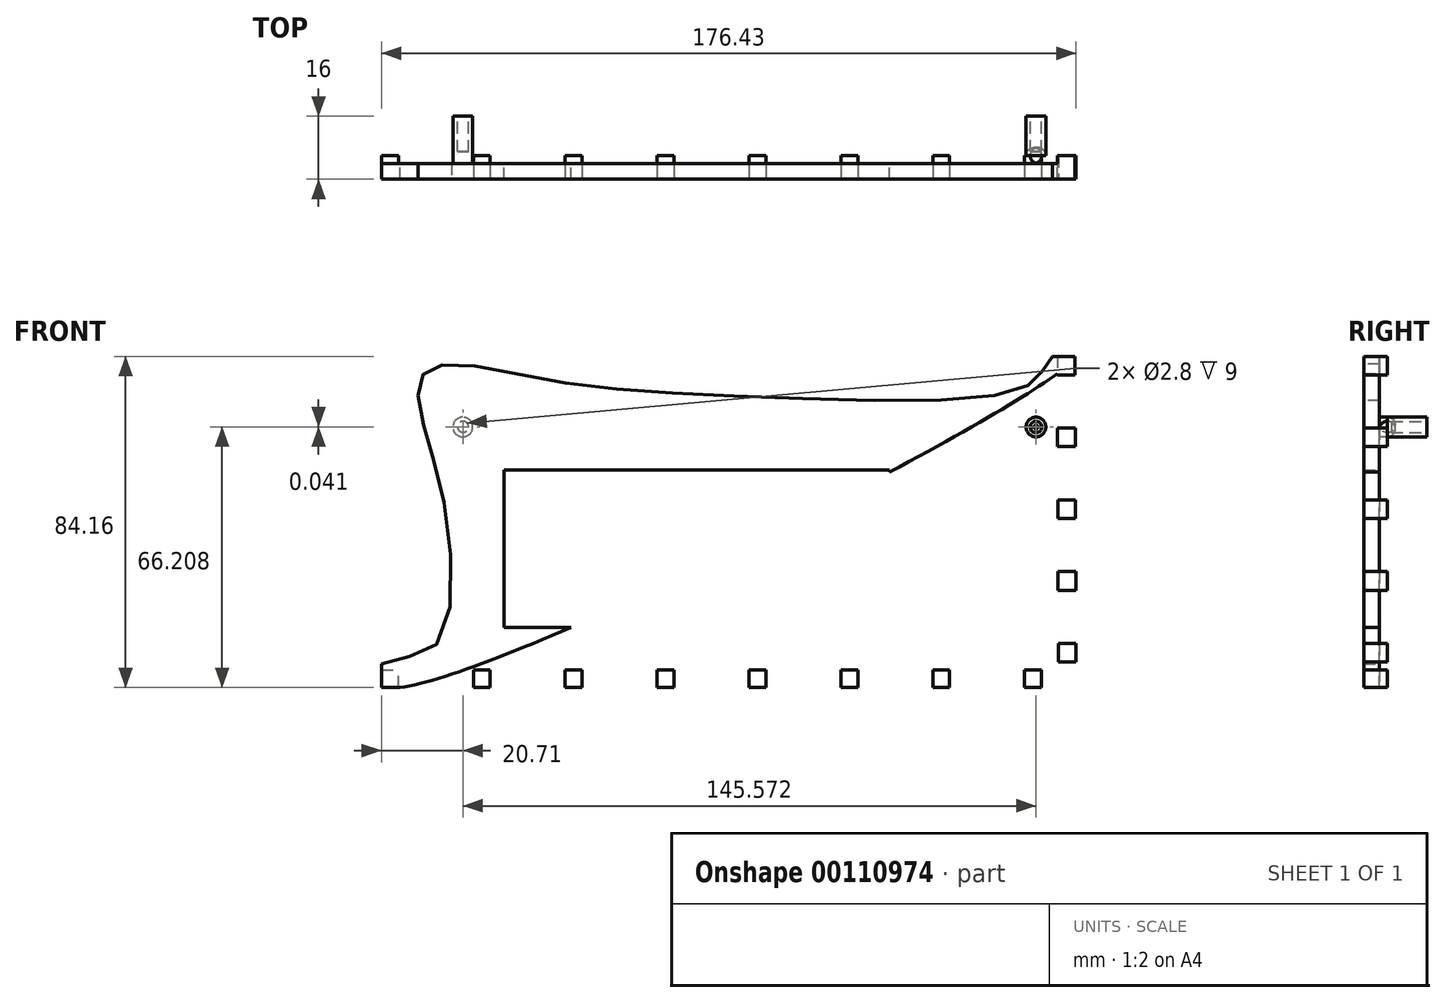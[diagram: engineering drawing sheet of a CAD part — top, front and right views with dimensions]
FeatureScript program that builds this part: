
annotation { "Feature Type Name" : "Feature", "Feature Type Description" : "" }
export const myFeature = defineFeature(function(context is Context, id is Id, definition is map)
    precondition{}
    {
        {
            var Q0;
            Q0=qCreatedBy(makeId("Front.planeOp"),FACE);
            var sketch = newSketch(context, id + "F0", { "sketchPlane" : qUnion([Q0])});
            skLineSegment(sketch, "E0.bottom", {"start": v(-77.31, 21.96) * mm, "end": v(72.69, 21.96) * mm, "construction": true});
            skLineSegment(sketch, "E0.top", {"start": v(-77.31, -41.04) * mm, "end": v(72.69, -41.04) * mm, "construction": true});
            skLineSegment(sketch, "E0.left", {"start": v(-77.31, 21.96) * mm, "end": v(-77.31, -41.04) * mm, "construction": true});
            skLineSegment(sketch, "E0.right", {"start": v(72.69, 21.96) * mm, "end": v(72.69, -41.04) * mm, "construction": true});
            skLineSegment(sketch, "E1", {"start": v(-95.43, -46.36) * mm, "end": v(-95.43, -40.35) * mm});
            skLineSegment(sketch, "E2", {"start": v(80.76, 37.8) * mm, "end": v(75.04, 37.8) * mm});
            skFitSpline(sketch, "E3", {"points": [v(-95.43, -40.35) * mm, v(-82.26, -36.25) * mm, v(-78.93, -2.99) * mm, v(-85.2, 22.25) * mm, v(-85.4, 32.43) * mm, v(-78.74, 35.75) * mm, v(-51.35, 31.45) * mm, v(0, 27.48) * mm, v(63.48, 28.43) * mm, v(72.2, 33.55) * mm, v(75.04, 37.8) * mm, v(80.76, 37.8) * mm, v(-95.43, -46.36) * mm, v(-95.43, -40.35) * mm]});
            skLineSegment(sketch, "E4.bottom", {"start": v(-64.31, 8.96) * mm, "end": v(33.69, 8.96) * mm});
            skLineSegment(sketch, "E4.top", {"start": v(-64.31, -31.04) * mm, "end": v(33.69, -31.04) * mm});
            skLineSegment(sketch, "E4.left", {"start": v(-64.31, 8.96) * mm, "end": v(-64.31, -31.04) * mm});
            skLineSegment(sketch, "E4.right", {"start": v(33.69, 8.96) * mm, "end": v(33.69, -31.04) * mm});
            skCircle(sketch, "E5", {"center": v(59.69, -7.04) * mm, "radius": 4.55 * mm});
            skCircle(sketch, "E6", {"center": v(59.69, -26.04) * mm, "radius": 2.98 * mm});
            skLineSegment(sketch, "E7", {"start": v(72.81, -46.36) * mm, "end": v(72.81, -40.54) * mm});
            skLineSegment(sketch, "E8", {"start": v(72.81, -40.54) * mm, "end": v(80.76, -40.54) * mm});
            skLineSegment(sketch, "E9", {"start": v(-95.43, -46.36) * mm, "end": v(72.81, -46.36) * mm});
            skLineSegment(sketch, "E10", {"start": v(80.76, 37.8) * mm, "end": v(80.76, -40.54) * mm});
            skSolve(sketch);
        }
        {
            var Q0;
            {var subQ0=sQuery(id+"F0.wireOp",EDGE,"E1");Q0=makeQuery(id+"F0.imprint","IMPRINT",FACE,{"disambiguationData":[TD([[makeQuery(id+"F0.imprint","IMPRINT",EDGE,{"derivedFrom":subQ0}),-1.0]])]});}
            extrude(context, id + "F1", {"entities" : qUnion([Q0]), "depth" : 4 * mm});
        }
        {
            var Q0;
            Q0=makeQuery(id+"F1.opExtrude","CAP_FACE",FACE,{"disambiguationData":[OSD([sQuery(id+"F0.wireOp",EDGE,"KkOOTngl-gOGY-si4M-3crp-3VL3Vou1fvHf"),sQuery(id+"F0.wireOp",EDGE,"FOtoh2e2-dB42-D3HZ-a7s3-6A5ojptzeBmU"),sQuery(id+"F0.wireOp",EDGE,"E1"),sQuery(id+"F0.wireOp",EDGE,"E2"),sQuery(id+"F0.wireOp",EDGE,"E3"),sQuery(id+"F0.wireOp",EDGE,"E4.bottom"),sQuery(id+"F0.wireOp",EDGE,"E4.top"),sQuery(id+"F0.wireOp",EDGE,"E4.left"),sQuery(id+"F0.wireOp",EDGE,"E4.right"),sQuery(id+"F0.wireOp",EDGE,"E5"),sQuery(id+"F0.wireOp",EDGE,"E6"),sQuery(id+"F0.wireOp",EDGE,"Dp8yctgh-aOOT-2nYt-riCS-tyILgEhAp9Hk"),sQuery(id+"F0.wireOp",EDGE,"Cd0YMjuJ-as3f-gzYX-xIN0-BSwLhn0KXe4p")])],"isStart":false});
            var sketch = newSketch(context, id + "F2", { "sketchPlane" : qUnion([Q0])});
            skLineSegment(sketch, "E11.bottom", {"start": v(-95.43, -46.36) * mm, "end": v(-91.12, -46.36) * mm});
            skLineSegment(sketch, "E11.top", {"start": v(-95.43, -41.86) * mm, "end": v(-91.12, -41.86) * mm});
            skLineSegment(sketch, "E11.left", {"start": v(-95.43, -46.36) * mm, "end": v(-95.43, -41.86) * mm});
            skLineSegment(sketch, "E11.right", {"start": v(-91.12, -46.36) * mm, "end": v(-91.12, -41.86) * mm});
            skLineSegment(sketch, "E12.1.0.0", {"start": v(-67.78, -46.36) * mm, "end": v(-67.78, -41.86) * mm});
            skLineSegment(sketch, "E12.1.0.1", {"start": v(-72.09, -46.36) * mm, "end": v(-72.09, -41.86) * mm});
            skLineSegment(sketch, "E12.1.0.2", {"start": v(-72.09, -41.86) * mm, "end": v(-67.78, -41.86) * mm});
            skLineSegment(sketch, "E12.1.0.3", {"start": v(-72.09, -46.36) * mm, "end": v(-67.78, -46.36) * mm});
            skLineSegment(sketch, "E12.2.0.0", {"start": v(-44.44, -46.36) * mm, "end": v(-44.44, -41.86) * mm});
            skLineSegment(sketch, "E12.2.0.1", {"start": v(-48.74, -46.36) * mm, "end": v(-48.74, -41.86) * mm});
            skLineSegment(sketch, "E12.2.0.2", {"start": v(-48.74, -41.86) * mm, "end": v(-44.44, -41.86) * mm});
            skLineSegment(sketch, "E12.2.0.3", {"start": v(-48.74, -46.36) * mm, "end": v(-44.44, -46.36) * mm});
            skLineSegment(sketch, "E12.3.0.0", {"start": v(-21.1, -46.36) * mm, "end": v(-21.1, -41.86) * mm});
            skLineSegment(sketch, "E12.3.0.1", {"start": v(-25.4, -46.36) * mm, "end": v(-25.4, -41.86) * mm});
            skLineSegment(sketch, "E12.3.0.2", {"start": v(-25.4, -41.86) * mm, "end": v(-21.1, -41.86) * mm});
            skLineSegment(sketch, "E12.3.0.3", {"start": v(-25.4, -46.36) * mm, "end": v(-21.1, -46.36) * mm});
            skLineSegment(sketch, "E12.4.0.0", {"start": v(2.24, -46.36) * mm, "end": v(2.24, -41.86) * mm});
            skLineSegment(sketch, "E12.4.0.1", {"start": v(-2.06, -46.36) * mm, "end": v(-2.06, -41.86) * mm});
            skLineSegment(sketch, "E12.4.0.2", {"start": v(-2.06, -41.86) * mm, "end": v(2.24, -41.86) * mm});
            skLineSegment(sketch, "E12.4.0.3", {"start": v(-2.06, -46.36) * mm, "end": v(2.24, -46.36) * mm});
            skLineSegment(sketch, "E12.5.0.0", {"start": v(25.59, -46.36) * mm, "end": v(25.59, -41.86) * mm});
            skLineSegment(sketch, "E12.5.0.1", {"start": v(21.28, -46.36) * mm, "end": v(21.28, -41.86) * mm});
            skLineSegment(sketch, "E12.5.0.2", {"start": v(21.28, -41.86) * mm, "end": v(25.59, -41.86) * mm});
            skLineSegment(sketch, "E12.5.0.3", {"start": v(21.28, -46.36) * mm, "end": v(25.59, -46.36) * mm});
            skLineSegment(sketch, "E12.6.0.0", {"start": v(48.93, -46.36) * mm, "end": v(48.93, -41.86) * mm});
            skLineSegment(sketch, "E12.6.0.1", {"start": v(44.62, -46.36) * mm, "end": v(44.62, -41.86) * mm});
            skLineSegment(sketch, "E12.6.0.2", {"start": v(44.62, -41.86) * mm, "end": v(48.93, -41.86) * mm});
            skLineSegment(sketch, "E12.6.0.3", {"start": v(44.62, -46.36) * mm, "end": v(48.93, -46.36) * mm});
            skLineSegment(sketch, "E12.7.0.0", {"start": v(72.27, -46.36) * mm, "end": v(72.27, -41.86) * mm});
            skLineSegment(sketch, "E12.7.0.1", {"start": v(67.97, -46.36) * mm, "end": v(67.97, -41.86) * mm});
            skLineSegment(sketch, "E12.7.0.2", {"start": v(67.97, -41.86) * mm, "end": v(72.27, -41.86) * mm});
            skLineSegment(sketch, "E12.7.0.3", {"start": v(67.97, -46.36) * mm, "end": v(72.27, -46.36) * mm});
            skLineSegment(sketch, "E12.direction1", {"start": v(-95.43, -46.36) * mm, "end": v(-72.09, -46.36) * mm, "construction": true});
            skLineSegment(sketch, "E13.bottom", {"start": v(80.76, 37.8) * mm, "end": v(76.26, 37.8) * mm});
            skLineSegment(sketch, "E13.top", {"start": v(80.76, 33.08) * mm, "end": v(76.26, 33.08) * mm});
            skLineSegment(sketch, "E13.left", {"start": v(80.76, 37.8) * mm, "end": v(80.76, 33.08) * mm});
            skLineSegment(sketch, "E13.right", {"start": v(76.26, 37.8) * mm, "end": v(76.26, 33.08) * mm});
            skLineSegment(sketch, "E14.1.0.0", {"start": v(80.82, 19.56) * mm, "end": v(80.82, 14.84) * mm});
            skLineSegment(sketch, "E14.1.0.1", {"start": v(80.82, 14.84) * mm, "end": v(76.32, 14.84) * mm});
            skLineSegment(sketch, "E14.1.0.2", {"start": v(80.82, 19.56) * mm, "end": v(76.32, 19.56) * mm});
            skLineSegment(sketch, "E14.1.0.3", {"start": v(76.32, 19.56) * mm, "end": v(76.32, 14.84) * mm});
            skLineSegment(sketch, "E14.2.0.0", {"start": v(80.88, 1.32) * mm, "end": v(80.88, -3.4) * mm});
            skLineSegment(sketch, "E14.2.0.1", {"start": v(80.88, -3.4) * mm, "end": v(76.38, -3.4) * mm});
            skLineSegment(sketch, "E14.2.0.2", {"start": v(80.88, 1.32) * mm, "end": v(76.38, 1.32) * mm});
            skLineSegment(sketch, "E14.2.0.3", {"start": v(76.38, 1.32) * mm, "end": v(76.38, -3.4) * mm});
            skLineSegment(sketch, "E14.3.0.0", {"start": v(80.94, -16.92) * mm, "end": v(80.94, -21.64) * mm});
            skLineSegment(sketch, "E14.3.0.1", {"start": v(80.94, -21.64) * mm, "end": v(76.44, -21.64) * mm});
            skLineSegment(sketch, "E14.3.0.2", {"start": v(80.94, -16.92) * mm, "end": v(76.44, -16.92) * mm});
            skLineSegment(sketch, "E14.3.0.3", {"start": v(76.44, -16.92) * mm, "end": v(76.44, -21.64) * mm});
            skLineSegment(sketch, "E14.4.0.0", {"start": v(81, -35.16) * mm, "end": v(81, -39.88) * mm});
            skLineSegment(sketch, "E14.4.0.1", {"start": v(81, -39.88) * mm, "end": v(76.5, -39.88) * mm});
            skLineSegment(sketch, "E14.4.0.2", {"start": v(81, -35.16) * mm, "end": v(76.5, -35.16) * mm});
            skLineSegment(sketch, "E14.4.0.3", {"start": v(76.5, -35.16) * mm, "end": v(76.5, -39.88) * mm});
            skLineSegment(sketch, "E14.direction1", {"start": v(76.26, 33.08) * mm, "end": v(76.32, 14.84) * mm, "construction": true});
            skSolve(sketch);
        }
        {
            var Q0;
            Q0=qSketchRegion(id+"F2",true);
            extrude(context, id + "F3", {"entities" : qUnion([Q0]), "operationType" : NewBodyOperationType.ADD, "oppositeDirection" : true, "depth" : 6 * mm});
        }
        {
            var Q0;
            Q0=makeQuery(id+"F1.opExtrude","CAP_FACE",FACE,{"disambiguationData":[OSD([sQuery(id+"F0.wireOp",EDGE,"E1"),sQuery(id+"F0.wireOp",EDGE,"E2"),sQuery(id+"F0.wireOp",EDGE,"E3"),sQuery(id+"F0.wireOp",EDGE,"E4.bottom"),sQuery(id+"F0.wireOp",EDGE,"E4.top"),sQuery(id+"F0.wireOp",EDGE,"E4.left"),sQuery(id+"F0.wireOp",EDGE,"E4.right"),sQuery(id+"F0.wireOp",EDGE,"E5"),sQuery(id+"F0.wireOp",EDGE,"E6"),sQuery(id+"F0.wireOp",EDGE,"E7"),sQuery(id+"F0.wireOp",EDGE,"E8"),sQuery(id+"F0.wireOp",EDGE,"E9"),sQuery(id+"F0.wireOp",EDGE,"E10")])],"isStart":true});
            var sketch = newSketch(context, id + "F4", { "sketchPlane" : qUnion([Q0])});
            skCircle(sketch, "E15", {"center": v(-70.85, 19.85) * mm, "radius": 2.52 * mm});
            skCircle(sketch, "E16", {"center": v(74.76, 19.85) * mm, "radius": 2.52 * mm});
            skSolve(sketch);
        }
        {
            var Q0;
            Q0 = qSketchRegion(id + "F4", true);
            extrude(context, id + "F5", {"entities" : qUnion([Q0]), "operationType" : NewBodyOperationType.ADD, "depth" : 12 * mm});
        }
        {
            var Q0;
            Q0=makeQuery(id+"F5.opExtrude","CAP_FACE",FACE,{"disambiguationData":[OSD([sQuery(id+"F4.wireOp",EDGE,"E15")])],"isStart":false});
            var sketch = newSketch(context, id + "F6", { "sketchPlane" : qUnion([Q0])});
            skCircle(sketch, "E17", {"center": v(-70.85, 19.85) * mm, "radius": 1.4 * mm});
            skCircle(sketch, "E18", {"center": v(74.72, 19.89) * mm, "radius": 1.4 * mm});
            skSolve(sketch);
        }
        {
            var Q0;
            Q0 = qSketchRegion(id + "F6", true);
            extrude(context, id + "F7", {"entities" : qUnion([Q0]), "operationType" : NewBodyOperationType.REMOVE, "oppositeDirection" : true, "depth" : 9 * mm});
        }
        {
            var Q0;
            Q0=makeQuery(id+"F5.opExtrude","CAP_EDGE",EDGE,{"disambiguationData":[OSD([sQuery(id+"F4.wireOp",EDGE,"E15")])],"isStart":true});
            var Q1;
            Q1=makeQuery(id+"F5.opExtrude","CAP_EDGE",EDGE,{"disambiguationData":[OSD([sQuery(id+"F4.wireOp",EDGE,"E16")])],"isStart":true});
            fillet(context, id + "F8", {"entities" : qUnion([Q0, Q1]), "radius" : 2 * mm, "tangentPropagation" : true, "allowEdgeOverflow" : false});
        }
    });
